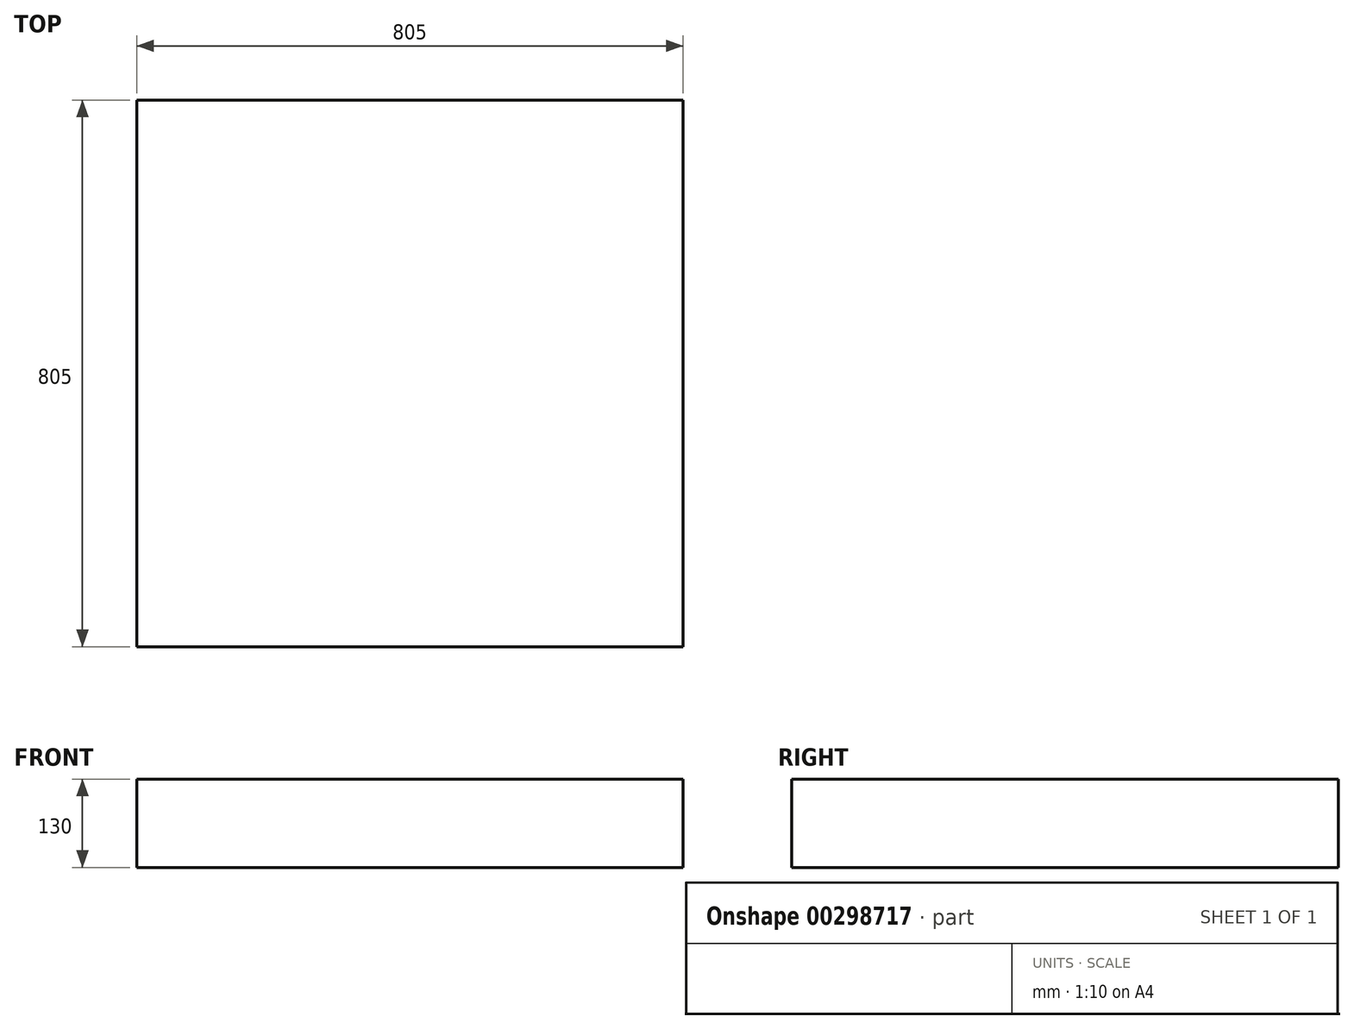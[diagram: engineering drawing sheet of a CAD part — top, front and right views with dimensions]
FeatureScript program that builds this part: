
annotation { "Feature Type Name" : "Feature", "Feature Type Description" : "" }
export const myFeature = defineFeature(function(context is Context, id is Id, definition is map)
    precondition{}
    {
        {
            var Q0;
            Q0=qCreatedBy(makeId("Top.planeOp"),FACE);
            var sketch = newSketch(context, id + "F0", { "sketchPlane" : qUnion([Q0])});
            skLineSegment(sketch, "E0.bottom", {"start": v(402.5, 402.5) * mm, "end": v(-402.5, 402.5) * mm});
            skLineSegment(sketch, "E0.top", {"start": v(402.5, -402.5) * mm, "end": v(-402.5, -402.5) * mm});
            skLineSegment(sketch, "E0.left", {"start": v(402.5, 402.5) * mm, "end": v(402.5, -402.5) * mm});
            skLineSegment(sketch, "E0.right", {"start": v(-402.5, 402.5) * mm, "end": v(-402.5, -402.5) * mm});
            skPoint(sketch, "E0.middle", {"position": v(0, 0) * mm});
            skSolve(sketch);
        }
        {
            var Q0;
            Q0=makeQuery(id+"F0.imprint","IMPRINT",FACE,{"disambiguationData":[TD([[makeQuery(id+"F0.imprint","IMPRINT",EDGE,{"derivedFrom":sQuery(id+"F0.wireOp",EDGE,"E0.bottom")}),1.0]])]});
            extrude(context, id + "F1", {"entities" : qUnion([Q0]), "depth" : 130 * mm});
        }
    });
